# Revit family: JOMA_Balksko kombi_Grundform 320
name_source: partatom
category: Structural Connections
revit_build: Autodesk Revit Structure 2012 (Build: 20110309_2315(x64)
units: mm (PartAtom-declared; Revit-internal decimal feet)

## types (8) — shared parameters
D = 40 mm  [stored 0.131234 ft]
Default Elevation = 1219 mm
E = 42 mm  [stored 0.137795 ft]
F = 78 mm  [stored 0.255906 ft]
Grundform 320 = Yes
Länk Joma Dimensioneringsverktyg = http://www.joma.se
Material = Varmförzinkad stålplåt
Typ = GRUNDFORM 320
X = 38 mm  [stored 0.124672 ft]
Y = 71 mm  [stored 0.23294 ft]

## per-type parameters (varying)
| type | A | B | Vikt |
| 5245137  45x137 | 45 mm  [stored 0.147638 ft] | 137 mm  [stored 0.449475 ft] | 0,37 |
| 5251135  51x135 | 51 mm | 135 mm  [stored 0.442913 ft] | 0,37 |
| 5260130  60x130 | 60 mm  [stored 0.19685 ft] | 130 mm  [stored 0.426509 ft] | 0,37 |
| 5270125  70x125 | 70 mm  [stored 0.229659 ft] | 125 mm  [stored 0.410105 ft] | 0,37 |
| 5276120  76x120 | 76 mm  [stored 0.249344 ft] | 122 mm  [stored 0.400262 ft] | 0,37 |
| 5280120  80x120 | 80 mm  [stored 0.262467 ft] | 120 mm  [stored 0.393701 ft] | 0,37 |
| 5236142  36x142 | 36 mm  [stored 0.11811 ft] | 142 mm  [stored 0.465879 ft] | 0,38 |
| 5248136  48x136 | 48 mm  [stored 0.15748 ft] | 136 mm | 0,37 |

note: [stored X ft] marks values corroborated as IEEE doubles in the binary element streams (Revit-internal decimal feet)

## geometry (parser evidence)
native form markers: Sweep x2
no freeform markers — native parametric forms only
